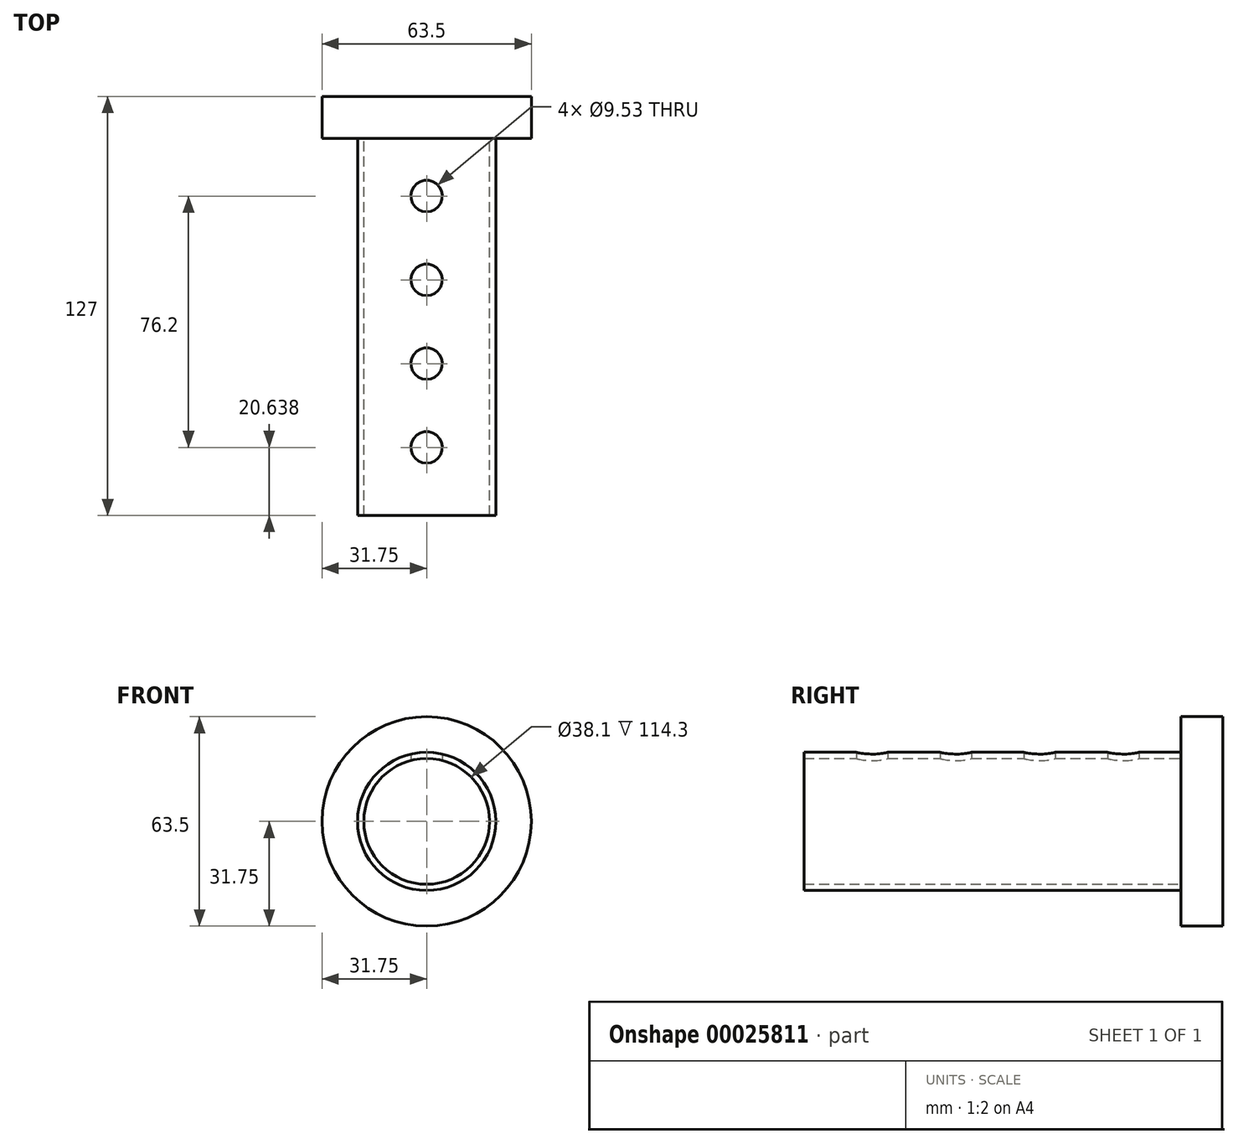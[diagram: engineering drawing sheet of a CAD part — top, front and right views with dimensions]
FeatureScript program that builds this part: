
annotation { "Feature Type Name" : "Feature", "Feature Type Description" : "" }
export const myFeature = defineFeature(function(context is Context, id is Id, definition is map)
    precondition{}
    {
        {
            var Q0;
            Q0=qCreatedBy(makeId("Front.planeOp"),FACE);
            var sketch = newSketch(context, id + "F0", { "sketchPlane" : qUnion([Q0])});
            skCircle(sketch, "E0", {"center": v(0, 0) * mm, "radius": 31.75 * mm});
            skSolve(sketch);
        }
        {
            var Q0;
            Q0=makeQuery(id+"F0.imprint","IMPRINT",FACE,{"disambiguationData":[TD([[makeQuery(id+"F0.imprint","IMPRINT",EDGE,{"derivedFrom":sQuery(id+"F0.wireOp",EDGE,"E0")}),1.0]])]});
            extrude(context, id + "F1", {"entities" : qUnion([Q0]), "depth" : 12.7 * mm});
        }
        {
            var Q0;
            Q0=makeQuery(id+"F1.opExtrude","CAP_FACE",FACE,{"disambiguationData":[OSD([sQuery(id+"F0.wireOp",EDGE,"E0")])],"isStart":false});
            var sketch = newSketch(context, id + "F2", { "sketchPlane" : qUnion([Q0])});
            skCircle(sketch, "E1", {"center": v(0, 0) * mm, "radius": 19.05 * mm});
            skCircle(sketch, "E2", {"center": v(0, 0) * mm, "radius": 20.96 * mm});
            skSolve(sketch);
        }
        {
            var Q0;
            Q0=makeQuery(id+"F2.imprint","IMPRINT",FACE,{"disambiguationData":[TD([[makeQuery(id+"F2.imprint","IMPRINT",EDGE,{"derivedFrom":sQuery(id+"F2.wireOp",EDGE,"E1")}),-1.0]])]});
            extrude(context, id + "F3", {"entities" : qUnion([Q0]), "operationType" : NewBodyOperationType.ADD, "depth" : 114.3 * mm});
        }
        {
            var Q0;
            Q0=qCreatedBy(makeId("Top.planeOp"),FACE);
            var sketch = newSketch(context, id + "F4", { "sketchPlane" : qUnion([Q0])});
            skCircle(sketch, "E3", {"center": v(0, -30.16) * mm, "radius": 4.76 * mm});
            skCircle(sketch, "E4", {"center": v(0, -55.56) * mm, "radius": 4.76 * mm});
            skCircle(sketch, "E5", {"center": v(0, -80.96) * mm, "radius": 4.76 * mm});
            skCircle(sketch, "E6", {"center": v(0, -106.36) * mm, "radius": 4.76 * mm});
            skSolve(sketch);
        }
        {
            var Q0;
            Q0=makeQuery(id+"F4.imprint","IMPRINT",FACE,{"disambiguationData":[TD([[makeQuery(id+"F4.imprint","IMPRINT",EDGE,{"derivedFrom":sQuery(id+"F4.wireOp",EDGE,"E3")}),1.0]])]});
            var Q1;
            Q1=makeQuery(id+"F4.imprint","IMPRINT",FACE,{"disambiguationData":[TD([[makeQuery(id+"F4.imprint","IMPRINT",EDGE,{"derivedFrom":sQuery(id+"F4.wireOp",EDGE,"E4")}),1.0]])]});
            var Q2;
            Q2=makeQuery(id+"F4.imprint","IMPRINT",FACE,{"disambiguationData":[TD([[makeQuery(id+"F4.imprint","IMPRINT",EDGE,{"derivedFrom":sQuery(id+"F4.wireOp",EDGE,"E5")}),1.0]])]});
            var Q3;
            Q3=makeQuery(id+"F4.imprint","IMPRINT",FACE,{"disambiguationData":[TD([[makeQuery(id+"F4.imprint","IMPRINT",EDGE,{"derivedFrom":sQuery(id+"F4.wireOp",EDGE,"E6")}),1.0]])]});
            extrude(context, id + "F5", {"entities" : qUnion([Q0, Q1, Q2, Q3]), "operationType" : NewBodyOperationType.REMOVE, "depth" : 25.4 * mm});
        }
    });
